# Revit family: m7114_h320_single_lever_kitchen_mixer_320_with_pull_out_spout_73812800
name_source: partatom
category: Plumbing Fixtures
revit_build: Autodesk Revit 2015 (Build: 20140903_1530(x64)
units: mm (PartAtom-declared; Revit-internal decimal feet)

## types (1)
- Stainless Steel Optic
    BIMobject category = Taps & Mixers
    BIMobject category code = kitchen-taps
    BIMobject main category = Kitchen
    BIMobject main category code = kitchen
    BOSUseNativeGeometries = 1
    Brand url = http://www.hansgrohe-int.com
    Default Elevation = 4' - 0"
    Design country = Germany
    EAN code = https://4059625017487
    Edition number = 1
    IFC Classification = Sanitary Terminal
    Installation instructions = https://pro.hansgrohe-int.com
    Manufacturer country = Germany
    Manufacturer name = hansgrohe
    Masterformat 2014 Code = 11 30 13.13
    Masterformat 2014 Description = Residential Kitchen Appliances
    NBS Reference Code = 31-75
    NBS Reference Description = Sanitary Accessories
    Nominal height = 0
    Nominal width = 0
    OmniClass Code = 23-31 11 00
    OmniClass Description = Faucets
    Product Guid = 0804688f-623b-43d9-bed0-e016a34dee8a
    Product SKU = 73812800
    Product data url = https://bimobject.com
    Product family = M71
    Product group = Kitchen mixers
    Product name = M7114-H320 single lever kitchen mixer 320 with pull-out spout 73812800
    Product url = https://pro.hansgrohe-int.com
    QR code = http://bimobject.com
    Technical description = https://pro.hansgrohe-int.com
    UNSPSC Code = 301815
    Uniclass 1.4 Code = L725111
    Uniclass 1.4 Description = Mixer taps
    Uniclass 2.0 Code = PR-31-75
    Uniclass 2.0 Description = Sanitary Accessories
    Uniclass 2015 Code = Pr_40_20_87_84
    Uniclass 2015 Name = Sink taps
    Weight Net (Kg) = 0

## geometry (parser evidence)
native form markers: Sweep x2
no freeform markers — native parametric forms only
